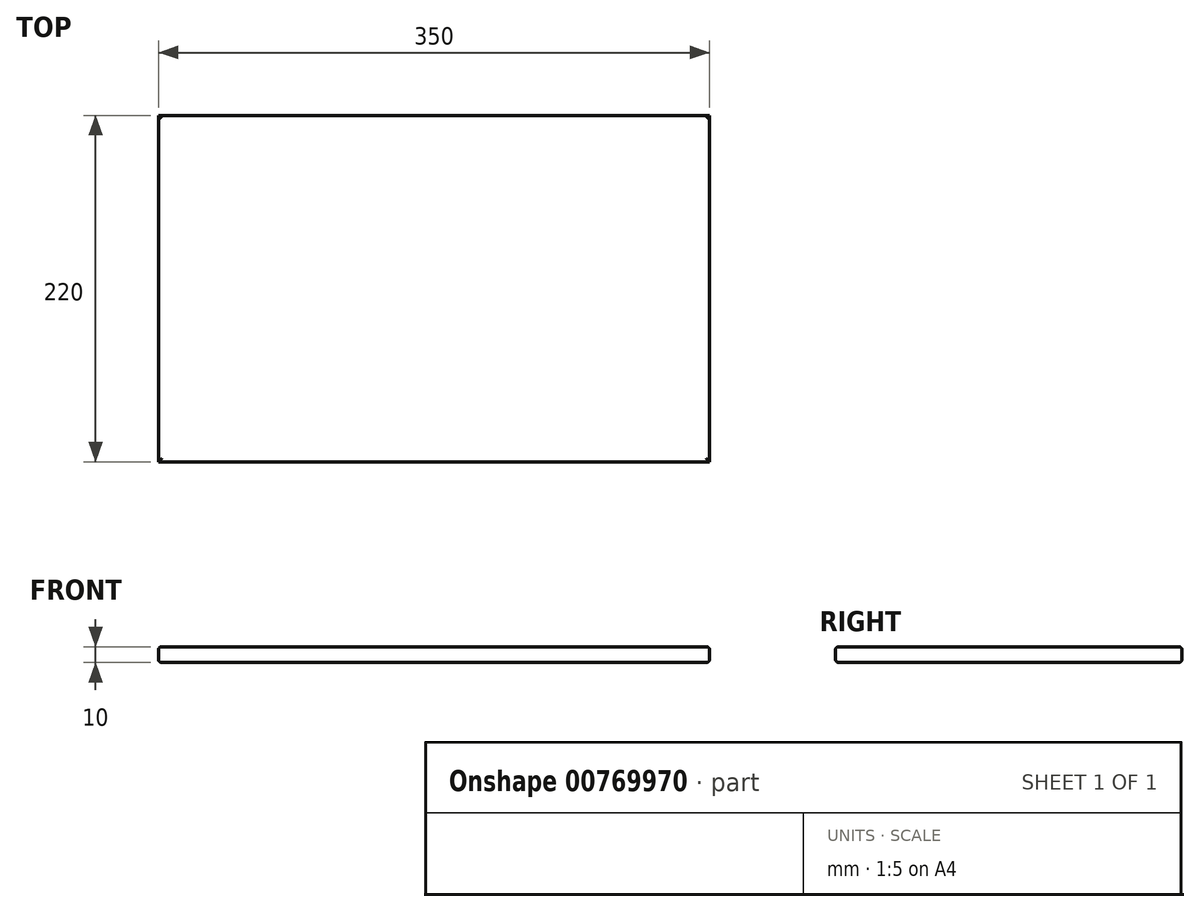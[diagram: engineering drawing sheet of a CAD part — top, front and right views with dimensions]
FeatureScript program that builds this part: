
annotation { "Feature Type Name" : "Feature", "Feature Type Description" : "" }
export const myFeature = defineFeature(function(context is Context, id is Id, definition is map)
    precondition{}
    {
        {
            var Q0;
            Q0=qCreatedBy(makeId("Top.planeOp"),FACE);
            var sketch = newSketch(context, id + "F0", { "sketchPlane" : qUnion([Q0])});
            skLineSegment(sketch, "E0.bottom", {"start": v(-70.88, 165.76) * mm, "end": v(279.12, 165.76) * mm});
            skLineSegment(sketch, "E0.top", {"start": v(-70.88, -54.24) * mm, "end": v(279.12, -54.24) * mm});
            skLineSegment(sketch, "E0.left", {"start": v(-70.88, 165.76) * mm, "end": v(-70.88, -54.24) * mm});
            skLineSegment(sketch, "E0.right", {"start": v(279.12, 165.76) * mm, "end": v(279.12, -54.24) * mm});
            skSolve(sketch);
        }
        {
            var Q0;
            Q0=makeQuery(id+"F0.imprint","IMPRINT",FACE,{"disambiguationData":[TD([[makeQuery(id+"F0.imprint","IMPRINT",EDGE,{"derivedFrom":sQuery(id+"F0.wireOp",EDGE,"E0.bottom")}),-1.0]])]});
            extrude(context, id + "F1", {"entities" : qUnion([Q0]), "depth" : 10 * mm, "offsetDistance" : 25 * mm});
        }
        {
            var Q0;
            Q0=makeQuery(id+"F1.opExtrude","CAP_FACE",FACE,{"disambiguationData":[OSD([sQuery(id+"F0.wireOp",EDGE,"E0.bottom"),sQuery(id+"F0.wireOp",EDGE,"E0.top"),sQuery(id+"F0.wireOp",EDGE,"E0.left"),sQuery(id+"F0.wireOp",EDGE,"E0.right")])],"isStart":false});
            var Q1;
            Q1=makeQuery(id+"F1.opExtrude","CAP_FACE",FACE,{"disambiguationData":[OSD([sQuery(id+"F0.wireOp",EDGE,"E0.bottom"),sQuery(id+"F0.wireOp",EDGE,"E0.top"),sQuery(id+"F0.wireOp",EDGE,"E0.left"),sQuery(id+"F0.wireOp",EDGE,"E0.right")])],"isStart":true});
            fillet(context, id + "F2", {"entities" : qUnion([Q0, Q1]), "radius" : 2 * mm, "tangentPropagation" : true, "allowEdgeOverflow" : false});
        }
    });
